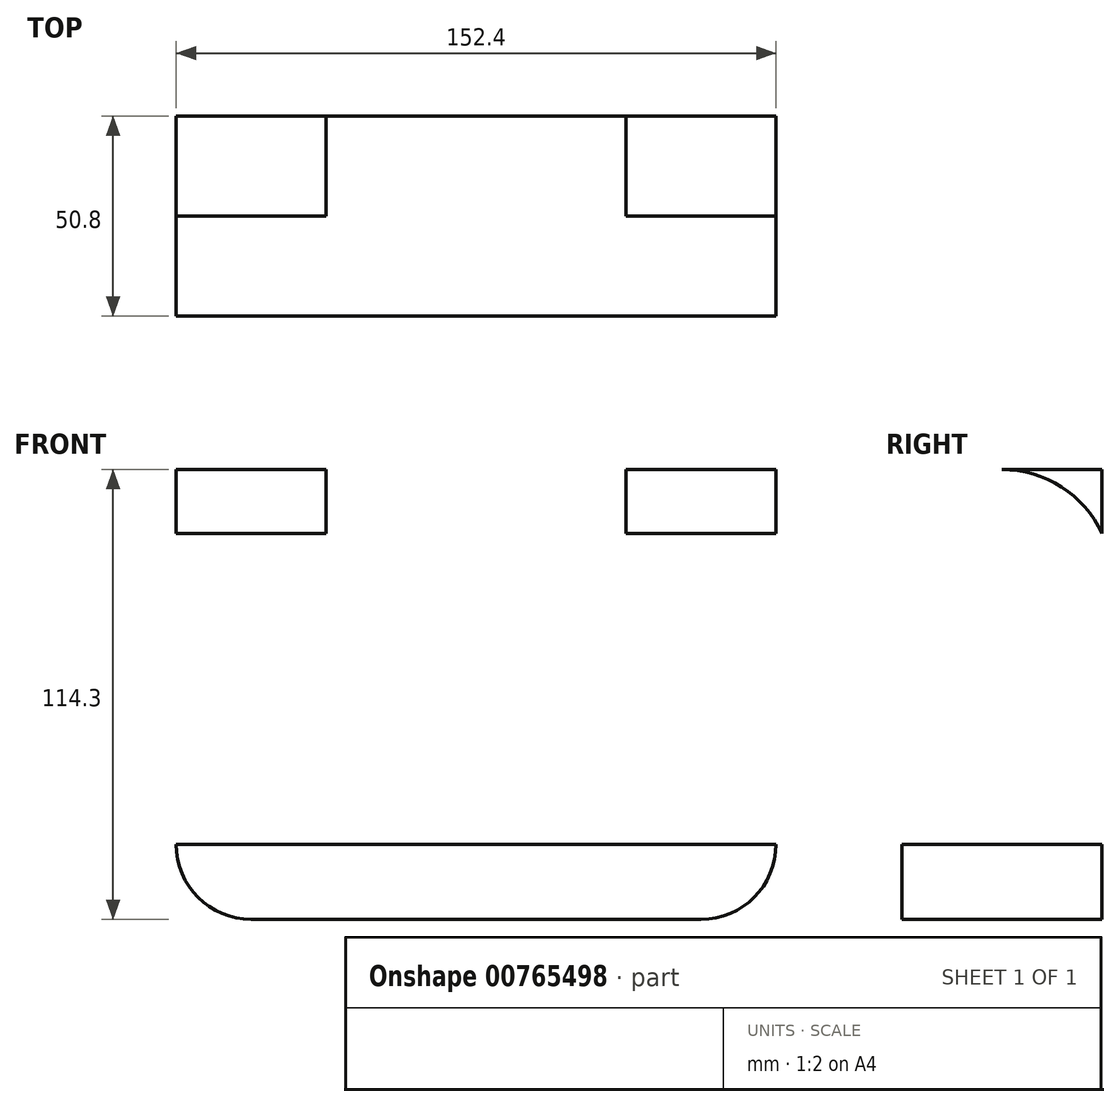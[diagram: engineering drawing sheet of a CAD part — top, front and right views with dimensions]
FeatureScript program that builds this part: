
annotation { "Feature Type Name" : "Feature", "Feature Type Description" : "" }
export const myFeature = defineFeature(function(context is Context, id is Id, definition is map)
    precondition{}
    {
        {
            var Q0;
            Q0=qCreatedBy(makeId("Front.planeOp"),FACE);
            var sketch = newSketch(context, id + "F0", { "sketchPlane" : qUnion([Q0])});
            skLineSegment(sketch, "E0.bottom", {"start": v(0, 0) * mm, "end": v(57.15, 0) * mm});
            skLineSegment(sketch, "E0.top", {"start": v(0, 38.1) * mm, "end": v(38.1, 38.1) * mm});
            skLineSegment(sketch, "E0.left", {"start": v(0, 0) * mm, "end": v(0, 38.1) * mm});
            skLineSegment(sketch, "E0.right", {"start": v(76.2, 0) * mm, "end": v(76.2, 38.1) * mm});
            skLineSegment(sketch, "E1.bottom", {"start": v(57.15, 0) * mm, "end": v(38.1, 0) * mm});
            skLineSegment(sketch, "E1.top", {"start": v(76.2, 114.3) * mm, "end": v(38.1, 114.3) * mm});
            skLineSegment(sketch, "E1.left", {"start": v(76.2, 38.1) * mm, "end": v(76.2, 114.3) * mm});
            skLineSegment(sketch, "E1.right", {"start": v(38.1, 38.1) * mm, "end": v(38.1, 114.3) * mm});
            skArc(sketch, "E2", {"start": v(57.15, 0) * mm, "mid": v(70.62, 5.58) * mm, "end": v(76.2, 19.05) * mm});
            skPoint(sketch, "E2.centerSnap0", {"position": v(76.2, 19.05) * mm});
            skPoint(sketch, "E2.centerSnap1", {"position": v(57.15, 114.3) * mm});
            skSolve(sketch);
        }
        {
            var Q0;
            Q0=makeQuery(id+"F0.imprint","IMPRINT",FACE,{"disambiguationData":[TD([[makeQuery(id+"F0.imprint","IMPRINT",EDGE,{"derivedFrom":sQuery(id+"F0.wireOp",EDGE,"E0.bottom")}),1.0]])]});
            extrude(context, id + "F1", {"entities" : qUnion([Q0]), "endBound" : BoundingType.SYMMETRIC, "depth" : 50.8 * mm, "offsetDistance" : 25.4 * mm});
        }
        {
            var Q0;
            Q0=makeQuery(id+"F1.opExtrude","SWEPT_BODY",BODY,{"disambiguationData":[OSD([sQuery(id+"F0.wireOp",EDGE,"E0.bottom"),sQuery(id+"F0.wireOp",EDGE,"E0.top"),sQuery(id+"F0.wireOp",EDGE,"E0.left"),sQuery(id+"F0.wireOp",EDGE,"E0.right"),sQuery(id+"F0.wireOp",EDGE,"E1.bottom"),sQuery(id+"F0.wireOp",EDGE,"E1.top"),sQuery(id+"F0.wireOp",EDGE,"E1.left"),sQuery(id+"F0.wireOp",EDGE,"E1.right"),sQuery(id+"F0.wireOp",EDGE,"E2")])]});
            var Q1;
            Q1=qCreatedBy(makeId("Right.planeOp"),FACE);
            mirror(context, id + "F2", {"operationType" : NewBodyOperationType.ADD, "entities" : qUnion([Q0]), "mirrorPlane" : qUnion([Q1])});
        }
        {
            var Q0;
            Q0=makeQuery(id+"F2.opPattern","COPY",FACE,{"derivedFrom":makeQuery(id+"F1.opExtrude","SWEPT_FACE",FACE,{"disambiguationData":[OSD([sQuery(id+"F0.wireOp",EDGE,"E0.right"),sQuery(id+"F0.wireOp",EDGE,"E1.left")])]}),"instanceName":"1"});
            var sketch = newSketch(context, id + "F3", { "sketchPlane" : qUnion([Q0])});
            skLineSegment(sketch, "E3", {"start": v(0, 114.3) * mm, "end": v(0, 95.25) * mm, "construction": true});
            skLineSegment(sketch, "E4.bottom", {"start": v(6.35, 88.9) * mm, "end": v(-6.35, 88.9) * mm});
            skLineSegment(sketch, "E4.top", {"start": v(6.35, 101.6) * mm, "end": v(-6.35, 101.6) * mm});
            skLineSegment(sketch, "E4.left", {"start": v(6.35, 88.9) * mm, "end": v(6.35, 101.6) * mm});
            skLineSegment(sketch, "E4.right", {"start": v(-6.35, 88.9) * mm, "end": v(-6.35, 101.6) * mm});
            skPoint(sketch, "E4.middle", {"position": v(0, 95.25) * mm});
            skArc(sketch, "E5", {"start": v(25.4, 98) * mm, "mid": v(15.1, 109.87) * mm, "end": v(0, 114.3) * mm});
            skArc(sketch, "E6.MirrorCS", {"start": v(-25.4, 98) * mm, "mid": v(-15.1, 109.87) * mm, "end": v(0, 114.3) * mm});
            skSolve(sketch);
        }
        {
            var Q0;
            {var subQ0=sQuery(id+"F3.wireOp",EDGE,"E6.MirrorCS");Q0=makeQuery(id+"F3.imprint","IMPRINT",FACE,{"disambiguationData":[TD([[makeQuery(id+"F3.imprint","IMPRINT",EDGE,{"derivedFrom":subQ0}),1.0]])]});}
            var Q1;
            {var subQ0=sQuery(id+"F3.wireOp",EDGE,"E5");Q1=makeQuery(id+"F3.imprint","IMPRINT",FACE,{"disambiguationData":[TD([[makeQuery(id+"F3.imprint","IMPRINT",EDGE,{"derivedFrom":subQ0}),-1.0]])]});}
            var Q2;
            Q2=makeQuery(id+"F3.imprint","IMPRINT",FACE,{"disambiguationData":[TD([[makeQuery(id+"F3.imprint","IMPRINT",EDGE,{"derivedFrom":sQuery(id+"F3.wireOp",EDGE,"E4.bottom")}),-1.0]])]});
            extrude(context, id + "F4", {"entities" : qUnion([Q0, Q1, Q2]), "operationType" : NewBodyOperationType.REMOVE, "endBound" : BoundingType.THROUGH_ALL, "oppositeDirection" : true, "depth" : 25.4 * mm, "offsetDistance" : 25.4 * mm});
        }
    });
